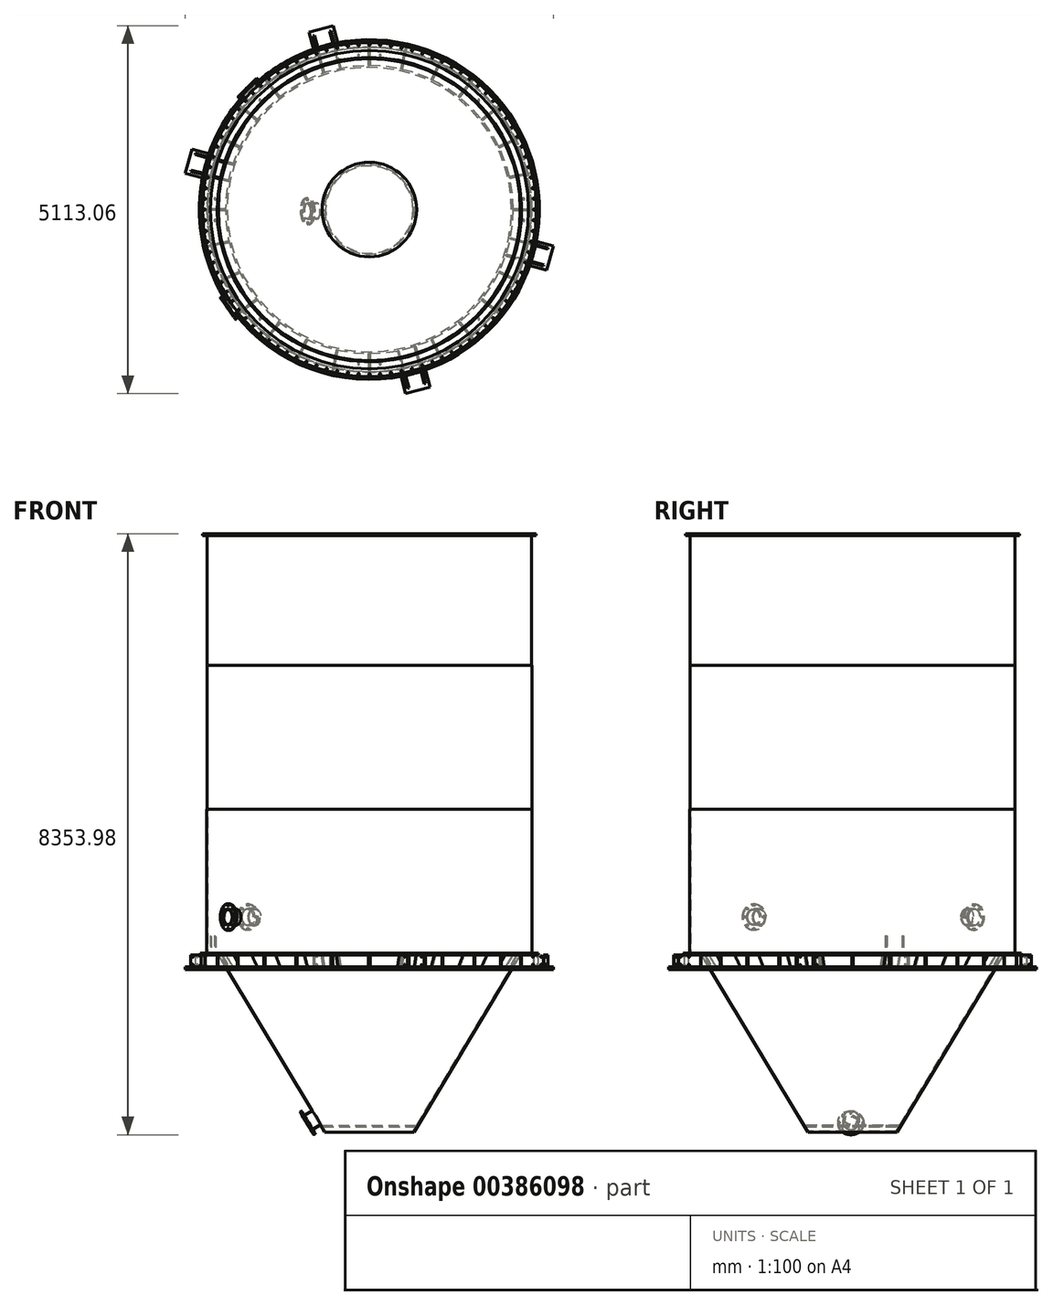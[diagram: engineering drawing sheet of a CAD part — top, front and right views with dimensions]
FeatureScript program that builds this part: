
annotation { "Feature Type Name" : "Feature", "Feature Type Description" : "" }
export const myFeature = defineFeature(function(context is Context, id is Id, definition is map)
    precondition{}
    {
        {
            var Q0;
            Q0=qCreatedBy(makeId("Front.planeOp"),FACE);
            var sketch = newSketch(context, id + "F0", { "sketchPlane" : qUnion([Q0])});
            skLineSegment(sketch, "E0", {"start": v(-2250, 0) * mm, "end": v(-2250, 5800) * mm});
            skLineSegment(sketch, "E1", {"start": v(-2256, 5800) * mm, "end": v(-2256, 4000) * mm});
            skLineSegment(sketch, "E2", {"start": v(-2256, 4000) * mm, "end": v(-2258, 4000) * mm});
            skLineSegment(sketch, "E3", {"start": v(-2258, 4000) * mm, "end": v(-2258, 2000) * mm});
            skLineSegment(sketch, "E4", {"start": v(-2258, 2000) * mm, "end": v(-2260, 2000) * mm});
            skLineSegment(sketch, "E5", {"start": v(-2260, 2000) * mm, "end": v(-2260, 0) * mm});
            skLineSegment(sketch, "E6", {"start": v(-2260, 0) * mm, "end": v(-2250, 0) * mm});
            skLineSegment(sketch, "E7", {"start": v(0, -16.96) * mm, "end": v(0, 862.75) * mm});
            skLineSegment(sketch, "E8", {"start": v(-2250, 5800) * mm, "end": v(-2212, 5800) * mm});
            skLineSegment(sketch, "E9", {"start": v(-2212, 5800) * mm, "end": v(-2212, 5828) * mm});
            skLineSegment(sketch, "E10", {"start": v(-2212, 5828) * mm, "end": v(-2320, 5828) * mm});
            skLineSegment(sketch, "E11", {"start": v(-2320, 5828) * mm, "end": v(-2320, 5800) * mm});
            skLineSegment(sketch, "E12", {"start": v(-2320, 5800) * mm, "end": v(-2256, 5800) * mm});
            skSolve(sketch);
        }
        {
            var Q0;
            Q0 = qSketchRegion(id + "F0", true);
            var Q1;
            Q1=sQuery(id+"F0.wireOp",EDGE,"E7");
            revolve(context, id + "F1", {"entities" : qUnion([Q0]), "axis" : qUnion([Q1]), "revolveType" : RevolveType.FULL});
        }
        {
            var Q0;
            Q0=qCreatedBy(makeId("Front.planeOp"),FACE);
            var sketch = newSketch(context, id + "F2", { "sketchPlane" : qUnion([Q0])});
            skLineSegment(sketch, "E13", {"start": v(-2350, 0) * mm, "end": v(-2115.02, 0) * mm});
            skLineSegment(sketch, "E14", {"start": v(-2115.02, 0) * mm, "end": v(-2100, -25) * mm});
            skLineSegment(sketch, "E15", {"start": v(-2100, -25) * mm, "end": v(-2350, -25) * mm});
            skLineSegment(sketch, "E16", {"start": v(-2350, -25) * mm, "end": v(-2350, 0) * mm});
            skLineSegment(sketch, "E17", {"start": v(0, -262.85) * mm, "end": v(0, -50.96) * mm});
            skSolve(sketch);
        }
        {
            var Q0;
            Q0 = qSketchRegion(id + "F2", true);
            var Q1;
            Q1=sQuery(id+"F2.wireOp",EDGE,"E17");
            revolve(context, id + "F3", {"operationType" : NewBodyOperationType.ADD, "entities" : qUnion([Q0]), "axis" : qUnion([Q1]), "revolveType" : RevolveType.FULL});
        }
        {
            var Q0;
            Q0=qCreatedBy(makeId("Front.planeOp"),FACE);
            var sketch = newSketch(context, id + "F4", { "sketchPlane" : qUnion([Q0])});
            skLineSegment(sketch, "E18", {"start": v(-2115.02, 0) * mm, "end": v(-620.5, -2487.3) * mm});
            skLineSegment(sketch, "E19", {"start": v(-607.64, -2479.58) * mm, "end": v(-2097.52, 0) * mm});
            skLineSegment(sketch, "E20", {"start": v(-2097.52, 0) * mm, "end": v(-2115.02, 0) * mm});
            skLineSegment(sketch, "E21", {"start": v(-620.5, -2487.3) * mm, "end": v(-607.64, -2479.58) * mm});
            skLineSegment(sketch, "E22", {"start": v(-647.98, -2412.44) * mm, "end": v(-657, -2397.44) * mm});
            skLineSegment(sketch, "E23", {"start": v(-657, -2397.44) * mm, "end": v(0, -2397.44) * mm});
            skLineSegment(sketch, "E24", {"start": v(0, -2397.44) * mm, "end": v(0, -2412.44) * mm});
            skLineSegment(sketch, "E25", {"start": v(0, -2412.44) * mm, "end": v(-647.98, -2412.44) * mm});
            skPoint(sketch, "E26", {"position": v(-1026, -1812.44) * mm});
            skSolve(sketch);
        }
        {
            var Q0;
            Q0 = qSketchRegion(id + "F4", true);
            var Q1;
            Q1=sQuery(id+"F0.wireOp",EDGE,"E7");
            revolve(context, id + "F5", {"entities" : qUnion([Q0]), "axis" : qUnion([Q1]), "revolveType" : RevolveType.FULL});
        }
        {
            var Q0;
            Q0=qCreatedBy(makeId("Front.planeOp"),FACE);
            var sketch = newSketch(context, id + "F6", { "sketchPlane" : qUnion([Q0])});
            skLineSegment(sketch, "E27", {"start": v(-2361.82, -190) * mm, "end": v(-2000.86, -190) * mm});
            skLineSegment(sketch, "E28", {"start": v(-2000.86, -190) * mm, "end": v(-1976.82, -230) * mm});
            skLineSegment(sketch, "E29", {"start": v(-1976.82, -230) * mm, "end": v(-2361.82, -230) * mm});
            skLineSegment(sketch, "E30", {"start": v(-2361.82, -230) * mm, "end": v(-2361.82, -190) * mm});
            skLineSegment(sketch, "E31", {"start": v(0, -406.67) * mm, "end": v(0, -308.21) * mm});
            skSolve(sketch);
        }
        {
            var Q0;
            Q0 = qSketchRegion(id + "F6", true);
            var Q1;
            Q1=sQuery(id+"F6.wireOp",EDGE,"E31");
            revolve(context, id + "F7", {"entities" : qUnion([Q0]), "axis" : qUnion([Q1]), "revolveType" : RevolveType.FULL});
        }
        {
            var Q0;
            Q0=qCreatedBy(makeId("Front.planeOp"),FACE);
            cPlane(context, id + "F8", {"entities" : qUnion([Q0]), "cplaneType" : CPlaneType.OFFSET, "offset" : 2340 * mm, "width" : 150 * mm, "height" : 150 * mm});
        }
        {
            var Q0;
            Q0=qCreatedBy(id+"F8.planeOp",FACE);
            var sketch = newSketch(context, id + "F9", { "sketchPlane" : qUnion([Q0])});
            skLineSegment(sketch, "E32", {"start": v(0, -25) * mm, "end": v(10, -25) * mm});
            skLineSegment(sketch, "E33", {"start": v(10, -25) * mm, "end": v(10, -190) * mm});
            skLineSegment(sketch, "E34", {"start": v(10, -190) * mm, "end": v(0, -190) * mm});
            skLineSegment(sketch, "E35", {"start": v(0, -190) * mm, "end": v(0, -25) * mm});
            skLineSegment(sketch, "E36.MirrorCS", {"start": v(-10, -190) * mm, "end": v(0, -190) * mm});
            skLineSegment(sketch, "E37.MirrorCS", {"start": v(0, -25) * mm, "end": v(-10, -25) * mm});
            skLineSegment(sketch, "E38.MirrorCS", {"start": v(-10, -25) * mm, "end": v(-10, -190) * mm});
            skSolve(sketch);
        }
        {
            var Q0;
            Q0=makeQuery(id+"F9.imprint","IMPRINT",FACE,{"disambiguationData":[TD([[makeQuery(id+"F9.imprint","IMPRINT",EDGE,{"derivedFrom":sQuery(id+"F9.wireOp",EDGE,"E32")}),-1.0]])]});
            var Q1;
            Q1=makeQuery(id+"F9.imprint","IMPRINT",FACE,{"disambiguationData":[TD([[makeQuery(id+"F9.imprint","IMPRINT",EDGE,{"derivedFrom":sQuery(id+"F9.wireOp",EDGE,"E35")}),1.0]])]});
            var Q2;
            Q2=makeQuery(id+"F5.opRevolve","SWEPT_FACE",FACE,{"disambiguationData":[OSD([sQuery(id+"F4.wireOp",EDGE,"E18")])]});
            extrude(context, id + "F10", {"entities" : qUnion([Q0, Q1]), "endBound" : BoundingType.UP_TO_SURFACE, "oppositeDirection" : true, "endBoundEntityFace" : qUnion([Q2]), "depth" : 25 * mm});
        }
        {
            var Q0;
            Q0=makeQuery(id+"F10.opExtrude","SWEPT_BODY",BODY,{"disambiguationData":[OSD([sQuery(id+"F9.wireOp",EDGE,"E32"),sQuery(id+"F9.wireOp",EDGE,"E33"),sQuery(id+"F9.wireOp",EDGE,"E34"),sQuery(id+"F9.wireOp",EDGE,"E36.MirrorCS"),sQuery(id+"F9.wireOp",EDGE,"E37.MirrorCS"),sQuery(id+"F9.wireOp",EDGE,"E38.MirrorCS")])]});
            var Q1;
            Q1=sQuery(id+"F0.wireOp",EDGE,"E7");
            circularPattern(context, id + "F11", {"entities" : qUnion([Q0]), "axis" : qUnion([Q1]), "angle" : 360 * degree, "instanceCount" : 28, "equalSpace" : true});
        }
        {
            var Q0;
            Q0=makeQuery(id+"F1.opRevolve","SWEPT_FACE",FACE,{"disambiguationData":[OSD([sQuery(id+"F0.wireOp",EDGE,"E10")])]});
            var sketch = newSketch(context, id + "F12", { "sketchPlane" : qUnion([Q0])});
            skCircle(sketch, "E39", {"center": v(-2290, 0) * mm, "radius": 10 * mm});
            skCircle(sketch, "E40.1.0", {"center": v(-2285.1, -149.77) * mm, "radius": 10 * mm});
            skCircle(sketch, "E40.2.0", {"center": v(-2270.4, -298.9) * mm, "radius": 10 * mm});
            skCircle(sketch, "E40.3.0", {"center": v(-2246, -446.76) * mm, "radius": 10 * mm});
            skCircle(sketch, "E40.4.0", {"center": v(-2211.97, -592.7) * mm, "radius": 10 * mm});
            skCircle(sketch, "E40.5.0", {"center": v(-2168.47, -736.1) * mm, "radius": 10 * mm});
            skCircle(sketch, "E40.6.0", {"center": v(-2115.68, -876.35) * mm, "radius": 10 * mm});
            skCircle(sketch, "E40.7.0", {"center": v(-2053.84, -1012.84) * mm, "radius": 10 * mm});
            skCircle(sketch, "E40.8.0", {"center": v(-1983.2, -1145) * mm, "radius": 10 * mm});
            skCircle(sketch, "E40.9.0", {"center": v(-1904.07, -1272.26) * mm, "radius": 10 * mm});
            skCircle(sketch, "E40.10.0", {"center": v(-1816.78, -1394.06) * mm, "radius": 10 * mm});
            skCircle(sketch, "E40.11.0", {"center": v(-1721.71, -1509.9) * mm, "radius": 10 * mm});
            skCircle(sketch, "E40.12.0", {"center": v(-1619.27, -1619.27) * mm, "radius": 10 * mm});
            skCircle(sketch, "E40.13.0", {"center": v(-1509.9, -1721.71) * mm, "radius": 10 * mm});
            skCircle(sketch, "E40.14.0", {"center": v(-1394.06, -1816.78) * mm, "radius": 10 * mm});
            skCircle(sketch, "E40.15.0", {"center": v(-1272.26, -1904.07) * mm, "radius": 10 * mm});
            skCircle(sketch, "E40.16.0", {"center": v(-1145, -1983.2) * mm, "radius": 10 * mm});
            skCircle(sketch, "E40.17.0", {"center": v(-1012.84, -2053.84) * mm, "radius": 10 * mm});
            skCircle(sketch, "E40.18.0", {"center": v(-876.35, -2115.68) * mm, "radius": 10 * mm});
            skCircle(sketch, "E40.19.0", {"center": v(-736.1, -2168.47) * mm, "radius": 10 * mm});
            skCircle(sketch, "E40.20.0", {"center": v(-592.7, -2211.97) * mm, "radius": 10 * mm});
            skCircle(sketch, "E40.21.0", {"center": v(-446.76, -2246) * mm, "radius": 10 * mm});
            skCircle(sketch, "E40.22.0", {"center": v(-298.9, -2270.4) * mm, "radius": 10 * mm});
            skCircle(sketch, "E40.23.0", {"center": v(-149.77, -2285.1) * mm, "radius": 10 * mm});
            skCircle(sketch, "E40.24.0", {"center": v(0, -2290) * mm, "radius": 10 * mm});
            skCircle(sketch, "E40.25.0", {"center": v(149.77, -2285.1) * mm, "radius": 10 * mm});
            skCircle(sketch, "E40.26.0", {"center": v(298.9, -2270.4) * mm, "radius": 10 * mm});
            skCircle(sketch, "E40.27.0", {"center": v(446.76, -2246) * mm, "radius": 10 * mm});
            skCircle(sketch, "E40.28.0", {"center": v(592.7, -2211.97) * mm, "radius": 10 * mm});
            skCircle(sketch, "E40.29.0", {"center": v(736.1, -2168.47) * mm, "radius": 10 * mm});
            skCircle(sketch, "E40.30.0", {"center": v(876.35, -2115.68) * mm, "radius": 10 * mm});
            skCircle(sketch, "E40.31.0", {"center": v(1012.84, -2053.84) * mm, "radius": 10 * mm});
            skCircle(sketch, "E40.32.0", {"center": v(1145, -1983.2) * mm, "radius": 10 * mm});
            skCircle(sketch, "E40.33.0", {"center": v(1272.26, -1904.07) * mm, "radius": 10 * mm});
            skCircle(sketch, "E40.34.0", {"center": v(1394.06, -1816.78) * mm, "radius": 10 * mm});
            skCircle(sketch, "E40.35.0", {"center": v(1509.9, -1721.71) * mm, "radius": 10 * mm});
            skCircle(sketch, "E40.36.0", {"center": v(1619.27, -1619.27) * mm, "radius": 10 * mm});
            skCircle(sketch, "E40.37.0", {"center": v(1721.71, -1509.9) * mm, "radius": 10 * mm});
            skCircle(sketch, "E40.38.0", {"center": v(1816.78, -1394.06) * mm, "radius": 10 * mm});
            skCircle(sketch, "E40.39.0", {"center": v(1904.07, -1272.26) * mm, "radius": 10 * mm});
            skCircle(sketch, "E40.40.0", {"center": v(1983.2, -1145) * mm, "radius": 10 * mm});
            skCircle(sketch, "E40.41.0", {"center": v(2053.84, -1012.84) * mm, "radius": 10 * mm});
            skCircle(sketch, "E40.42.0", {"center": v(2115.68, -876.35) * mm, "radius": 10 * mm});
            skCircle(sketch, "E40.43.0", {"center": v(2168.47, -736.1) * mm, "radius": 10 * mm});
            skCircle(sketch, "E40.44.0", {"center": v(2211.97, -592.7) * mm, "radius": 10 * mm});
            skCircle(sketch, "E40.45.0", {"center": v(2246, -446.76) * mm, "radius": 10 * mm});
            skCircle(sketch, "E40.46.0", {"center": v(2270.4, -298.9) * mm, "radius": 10 * mm});
            skCircle(sketch, "E40.47.0", {"center": v(2285.1, -149.77) * mm, "radius": 10 * mm});
            skCircle(sketch, "E40.48.0", {"center": v(2290, 0) * mm, "radius": 10 * mm});
            skCircle(sketch, "E40.49.0", {"center": v(2285.1, 149.77) * mm, "radius": 10 * mm});
            skCircle(sketch, "E40.50.0", {"center": v(2270.4, 298.9) * mm, "radius": 10 * mm});
            skCircle(sketch, "E40.51.0", {"center": v(2246, 446.76) * mm, "radius": 10 * mm});
            skCircle(sketch, "E40.52.0", {"center": v(2211.97, 592.7) * mm, "radius": 10 * mm});
            skCircle(sketch, "E40.53.0", {"center": v(2168.47, 736.1) * mm, "radius": 10 * mm});
            skCircle(sketch, "E40.54.0", {"center": v(2115.68, 876.35) * mm, "radius": 10 * mm});
            skCircle(sketch, "E40.55.0", {"center": v(2053.84, 1012.84) * mm, "radius": 10 * mm});
            skCircle(sketch, "E40.56.0", {"center": v(1983.2, 1145) * mm, "radius": 10 * mm});
            skCircle(sketch, "E40.57.0", {"center": v(1904.07, 1272.26) * mm, "radius": 10 * mm});
            skCircle(sketch, "E40.58.0", {"center": v(1816.78, 1394.06) * mm, "radius": 10 * mm});
            skCircle(sketch, "E40.59.0", {"center": v(1721.71, 1509.9) * mm, "radius": 10 * mm});
            skCircle(sketch, "E40.60.0", {"center": v(1619.27, 1619.27) * mm, "radius": 10 * mm});
            skCircle(sketch, "E40.61.0", {"center": v(1509.9, 1721.71) * mm, "radius": 10 * mm});
            skCircle(sketch, "E40.62.0", {"center": v(1394.06, 1816.78) * mm, "radius": 10 * mm});
            skCircle(sketch, "E40.63.0", {"center": v(1272.26, 1904.07) * mm, "radius": 10 * mm});
            skCircle(sketch, "E40.64.0", {"center": v(1145, 1983.2) * mm, "radius": 10 * mm});
            skCircle(sketch, "E40.65.0", {"center": v(1012.84, 2053.84) * mm, "radius": 10 * mm});
            skCircle(sketch, "E40.66.0", {"center": v(876.35, 2115.68) * mm, "radius": 10 * mm});
            skCircle(sketch, "E40.67.0", {"center": v(736.1, 2168.47) * mm, "radius": 10 * mm});
            skCircle(sketch, "E40.68.0", {"center": v(592.7, 2211.97) * mm, "radius": 10 * mm});
            skCircle(sketch, "E40.69.0", {"center": v(446.76, 2246) * mm, "radius": 10 * mm});
            skCircle(sketch, "E40.70.0", {"center": v(298.9, 2270.4) * mm, "radius": 10 * mm});
            skCircle(sketch, "E40.71.0", {"center": v(149.77, 2285.1) * mm, "radius": 10 * mm});
            skCircle(sketch, "E40.72.0", {"center": v(0, 2290) * mm, "radius": 10 * mm});
            skCircle(sketch, "E40.73.0", {"center": v(-149.77, 2285.1) * mm, "radius": 10 * mm});
            skCircle(sketch, "E40.74.0", {"center": v(-298.9, 2270.4) * mm, "radius": 10 * mm});
            skCircle(sketch, "E40.75.0", {"center": v(-446.76, 2246) * mm, "radius": 10 * mm});
            skCircle(sketch, "E40.76.0", {"center": v(-592.7, 2211.97) * mm, "radius": 10 * mm});
            skCircle(sketch, "E40.77.0", {"center": v(-736.1, 2168.47) * mm, "radius": 10 * mm});
            skCircle(sketch, "E40.78.0", {"center": v(-876.35, 2115.68) * mm, "radius": 10 * mm});
            skCircle(sketch, "E40.79.0", {"center": v(-1012.84, 2053.84) * mm, "radius": 10 * mm});
            skCircle(sketch, "E40.80.0", {"center": v(-1145, 1983.2) * mm, "radius": 10 * mm});
            skCircle(sketch, "E40.81.0", {"center": v(-1272.26, 1904.07) * mm, "radius": 10 * mm});
            skCircle(sketch, "E40.82.0", {"center": v(-1394.06, 1816.78) * mm, "radius": 10 * mm});
            skCircle(sketch, "E40.83.0", {"center": v(-1509.9, 1721.71) * mm, "radius": 10 * mm});
            skCircle(sketch, "E40.84.0", {"center": v(-1619.27, 1619.27) * mm, "radius": 10 * mm});
            skCircle(sketch, "E40.85.0", {"center": v(-1721.71, 1509.9) * mm, "radius": 10 * mm});
            skCircle(sketch, "E40.86.0", {"center": v(-1816.78, 1394.06) * mm, "radius": 10 * mm});
            skCircle(sketch, "E40.87.0", {"center": v(-1904.07, 1272.26) * mm, "radius": 10 * mm});
            skCircle(sketch, "E40.88.0", {"center": v(-1983.2, 1145) * mm, "radius": 10 * mm});
            skCircle(sketch, "E40.89.0", {"center": v(-2053.84, 1012.84) * mm, "radius": 10 * mm});
            skCircle(sketch, "E40.90.0", {"center": v(-2115.68, 876.35) * mm, "radius": 10 * mm});
            skCircle(sketch, "E40.91.0", {"center": v(-2168.47, 736.1) * mm, "radius": 10 * mm});
            skCircle(sketch, "E40.92.0", {"center": v(-2211.97, 592.7) * mm, "radius": 10 * mm});
            skCircle(sketch, "E40.93.0", {"center": v(-2246, 446.76) * mm, "radius": 10 * mm});
            skCircle(sketch, "E40.94.0", {"center": v(-2270.4, 298.9) * mm, "radius": 10 * mm});
            skCircle(sketch, "E40.95.0", {"center": v(-2285.1, 149.77) * mm, "radius": 10 * mm});
            skPoint(sketch, "E40.center", {"position": v(0, 0) * mm});
            skSolve(sketch);
        }
        {
            var Q0;
            Q0 = qSketchRegion(id + "F12", true);
            var Q1;
            Q1=makeQuery(id+"F1.opRevolve","SWEPT_FACE",FACE,{"disambiguationData":[OSD([sQuery(id+"F0.wireOp",EDGE,"E12")])]});
            extrude(context, id + "F13", {"entities" : qUnion([Q0]), "operationType" : NewBodyOperationType.REMOVE, "endBound" : BoundingType.UP_TO_SURFACE, "oppositeDirection" : true, "endBoundEntityFace" : qUnion([Q1]), "depth" : 25 * mm});
        }
        {
            var Q0;
            Q0=makeQuery(id+"F7.opRevolve","SWEPT_FACE",FACE,{"disambiguationData":[OSD([sQuery(id+"F6.wireOp",EDGE,"E27")])]});
            var sketch = newSketch(context, id + "F14", { "sketchPlane" : qUnion([Q0])});
            skCircle(sketch, "E41", {"center": v(-2144.76, 149.98) * mm, "radius": 12.5 * mm});
            skPoint(sketch, "E42", {"position": v(0, 0) * mm});
            skLineSegment(sketch, "E43", {"start": v(0, 0) * mm, "end": v(-2144.76, 149.98) * mm});
            skLineSegment(sketch, "E44", {"start": v(-2144.76, 0) * mm, "end": v(0, 0) * mm});
            skCircle(sketch, "E45.MirrorC", {"center": v(-2144.76, -149.98) * mm, "radius": 12.5 * mm});
            skCircle(sketch, "E46", {"center": v(-1520.28, 1520.28) * mm, "radius": 12.5 * mm});
            skLineSegment(sketch, "E47", {"start": v(-1520.28, 1520.28) * mm, "end": v(0, 0) * mm});
            skLineSegment(sketch, "E48.anchor1", {"start": v(0, 0) * mm, "end": v(-2144.76, -149.98) * mm, "construction": true});
            skCircle(sketch, "E49.1.0", {"center": v(-1520.28, -1520.28) * mm, "radius": 12.5 * mm});
            skCircle(sketch, "E49.1.1", {"center": v(-149.98, -2144.76) * mm, "radius": 12.5 * mm});
            skCircle(sketch, "E49.1.2", {"center": v(149.98, -2144.76) * mm, "radius": 12.5 * mm});
            skCircle(sketch, "E49.2.0", {"center": v(1520.28, -1520.28) * mm, "radius": 12.5 * mm});
            skCircle(sketch, "E49.2.1", {"center": v(2144.76, -149.98) * mm, "radius": 12.5 * mm});
            skCircle(sketch, "E49.2.2", {"center": v(2144.76, 149.98) * mm, "radius": 12.5 * mm});
            skCircle(sketch, "E49.3.0", {"center": v(1520.28, 1520.28) * mm, "radius": 12.5 * mm});
            skCircle(sketch, "E49.3.1", {"center": v(149.98, 2144.76) * mm, "radius": 12.5 * mm});
            skCircle(sketch, "E49.3.2", {"center": v(-149.98, 2144.76) * mm, "radius": 12.5 * mm});
            skPoint(sketch, "E50", {"position": v(-2000.17, -52.38) * mm});
            skLineSegment(sketch, "E51", {"start": v(0, 0) * mm, "end": v(-2000.17, -52.38) * mm, "construction": true});
            skPoint(sketch, "E52", {"position": v(-1843.1, -1290.55) * mm});
            skLineSegment(sketch, "E53", {"start": v(0, 0) * mm, "end": v(-1843.1, -1290.55) * mm, "construction": true});
            skLineSegment(sketch, "E54", {"start": v(-1843.1, -1290.55) * mm, "end": v(-1965.96, -1376.58) * mm});
            skSolve(sketch);
        }
        {
            var Q0;
            Q0 = qSketchRegion(id + "F14", true);
            var Q1;
            Q1=makeQuery(id+"F7.opRevolve","SWEPT_FACE",FACE,{"disambiguationData":[OSD([sQuery(id+"F6.wireOp",EDGE,"E29")])]});
            extrude(context, id + "F15", {"entities" : qUnion([Q0]), "operationType" : NewBodyOperationType.REMOVE, "endBound" : BoundingType.UP_TO_SURFACE, "oppositeDirection" : true, "endBoundEntityFace" : qUnion([Q1]), "depth" : 25 * mm});
        }
        {
            var Q0;
            Q0=makeQuery(id+"F11.opPattern","COPY",BODY,{"derivedFrom":makeQuery(id+"F10.opExtrude","SWEPT_BODY",BODY,{"disambiguationData":[OSD([sQuery(id+"F9.wireOp",EDGE,"E32"),sQuery(id+"F9.wireOp",EDGE,"E33"),sQuery(id+"F9.wireOp",EDGE,"E34"),sQuery(id+"F9.wireOp",EDGE,"E36.MirrorCS"),sQuery(id+"F9.wireOp",EDGE,"E37.MirrorCS"),sQuery(id+"F9.wireOp",EDGE,"E38.MirrorCS")])]}),"instanceName":"20"});
            deleteBodies(context, id + "F16", {"entities" : qUnion([Q0])});
        }
        {
            var Q0;
            Q0=makeQuery(id+"F11.opPattern","COPY",BODY,{"derivedFrom":makeQuery(id+"F10.opExtrude","SWEPT_BODY",BODY,{"disambiguationData":[OSD([sQuery(id+"F9.wireOp",EDGE,"E32"),sQuery(id+"F9.wireOp",EDGE,"E33"),sQuery(id+"F9.wireOp",EDGE,"E34"),sQuery(id+"F9.wireOp",EDGE,"E36.MirrorCS"),sQuery(id+"F9.wireOp",EDGE,"E37.MirrorCS"),sQuery(id+"F9.wireOp",EDGE,"E38.MirrorCS")])]}),"instanceName":"15"});
            deleteBodies(context, id + "F17", {"entities" : qUnion([Q0])});
        }
        {
            var Q0;
            Q0=makeQuery(id+"F11.opPattern","COPY",BODY,{"derivedFrom":makeQuery(id+"F10.opExtrude","SWEPT_BODY",BODY,{"disambiguationData":[OSD([sQuery(id+"F9.wireOp",EDGE,"E32"),sQuery(id+"F9.wireOp",EDGE,"E33"),sQuery(id+"F9.wireOp",EDGE,"E34"),sQuery(id+"F9.wireOp",EDGE,"E36.MirrorCS"),sQuery(id+"F9.wireOp",EDGE,"E37.MirrorCS"),sQuery(id+"F9.wireOp",EDGE,"E38.MirrorCS")])]}),"instanceName":"6"});
            deleteBodies(context, id + "F18", {"entities" : qUnion([Q0])});
        }
        {
            var Q0;
            Q0=makeQuery(id+"F11.opPattern","COPY",BODY,{"derivedFrom":makeQuery(id+"F10.opExtrude","SWEPT_BODY",BODY,{"disambiguationData":[OSD([sQuery(id+"F9.wireOp",EDGE,"E32"),sQuery(id+"F9.wireOp",EDGE,"E33"),sQuery(id+"F9.wireOp",EDGE,"E34"),sQuery(id+"F9.wireOp",EDGE,"E36.MirrorCS"),sQuery(id+"F9.wireOp",EDGE,"E37.MirrorCS"),sQuery(id+"F9.wireOp",EDGE,"E38.MirrorCS")])]}),"instanceName":"1"});
            deleteBodies(context, id + "F19", {"entities" : qUnion([Q0])});
        }
        {
            var Q0;
            Q0=makeQuery(id+"F14.imprint","IMPRINT",FACE,{"disambiguationData":[TD([[makeQuery(id+"F14.imprint","IMPRINT",EDGE,{"derivedFrom":sQuery(id+"F14.wireOp",EDGE,"E41")}),-1.0]])]});
            var sketch = newSketch(context, id + "F20", { "sketchPlane" : qUnion([Q0])});
            skLineSegment(sketch, "E55", {"start": v(-1894.95, 642.34) * mm, "end": v(-2417.87, 782.45) * mm});
            skLineSegment(sketch, "E56", {"start": v(-2417.87, 782.45) * mm, "end": v(-2423.05, 763.13) * mm});
            skLineSegment(sketch, "E57", {"start": v(-2423.05, 763.13) * mm, "end": v(-1901.29, 623.33) * mm});
            skLineSegment(sketch, "E58", {"start": v(0, 0) * mm, "end": v(-1901.45, 509.5) * mm, "construction": true});
            skArc(sketch, "E59", {"start": v(-1901.29, 623.33) * mm, "mid": v(-1898.14, 632.84) * mm, "end": v(-1894.95, 642.34) * mm});
            skLineSegment(sketch, "E60.MirrorCS", {"start": v(-2485.17, 531.31) * mm, "end": v(-2479.99, 550.63) * mm});
            skArc(sketch, "E61.MirrorCS", {"start": v(-1958.23, 410.83) * mm, "mid": v(-1960.26, 401.02) * mm, "end": v(-1962.24, 391.2) * mm});
            skLineSegment(sketch, "E62.MirrorCS", {"start": v(-2479.99, 550.63) * mm, "end": v(-1958.23, 410.83) * mm});
            skLineSegment(sketch, "E63.MirrorCS", {"start": v(-1962.24, 391.2) * mm, "end": v(-2485.17, 531.31) * mm});
            skSolve(sketch);
        }
        {
            var Q0;
            Q0 = qSketchRegion(id + "F20", true);
            var Q1;
            Q1=makeQuery(id+"F5.opRevolve","SWEPT_FACE",FACE,{"disambiguationData":[OSD([sQuery(id+"F4.wireOp",EDGE,"E18")])]});
            var Q2;
            Q2=makeQuery(id+"F1.opRevolve","SWEPT_BODY",BODY,{"disambiguationData":[OSD([sQuery(id+"F0.wireOp",EDGE,"E0"),sQuery(id+"F0.wireOp",EDGE,"E1"),sQuery(id+"F0.wireOp",EDGE,"E2"),sQuery(id+"F0.wireOp",EDGE,"E3"),sQuery(id+"F0.wireOp",EDGE,"E4"),sQuery(id+"F0.wireOp",EDGE,"E5"),sQuery(id+"F0.wireOp",EDGE,"E6"),sQuery(id+"F0.wireOp",EDGE,"E8"),sQuery(id+"F0.wireOp",EDGE,"E9"),sQuery(id+"F0.wireOp",EDGE,"E10"),sQuery(id+"F0.wireOp",EDGE,"E11"),sQuery(id+"F0.wireOp",EDGE,"E12")])]});
            extrude(context, id + "F21", {"entities" : qUnion([Q0]), "endBound" : BoundingType.UP_TO_SURFACE, "endBoundEntityFace" : qUnion([Q1]), "endBoundEntityBody" : qUnion([Q2]), "depth" : 25 * mm});
        }
        {
            var Q0;
            Q0=makeQuery(id+"F21.opExtrude","SWEPT_FACE",FACE,{"disambiguationData":[OSD([sQuery(id+"F20.wireOp",EDGE,"E55")])]});
            var sketch = newSketch(context, id + "F22", { "sketchPlane" : qUnion([Q0])});
            skLineSegment(sketch, "E64", {"start": v(2095.97, -25) * mm, "end": v(2538, 709.5) * mm});
            skLineSegment(sketch, "E65", {"start": v(2538, 709.5) * mm, "end": v(2538, -25) * mm});
            skLineSegment(sketch, "E66", {"start": v(2538, -25) * mm, "end": v(2095.97, -25) * mm});
            skSolve(sketch);
        }
        {
            var Q0;
            Q0 = qSketchRegion(id + "F22", true);
            var Q1;
            Q1=makeQuery(id+"F21.opExtrude","SWEPT_FACE",FACE,{"disambiguationData":[OSD([sQuery(id+"F20.wireOp",EDGE,"E57")])]});
            extrude(context, id + "F23", {"entities" : qUnion([Q0]), "operationType" : NewBodyOperationType.REMOVE, "endBound" : BoundingType.UP_TO_SURFACE, "oppositeDirection" : true, "endBoundEntityFace" : qUnion([Q1]), "depth" : 25 * mm});
        }
        {
            var Q0;
            Q0=makeQuery(id+"F21.opExtrude","SWEPT_FACE",FACE,{"disambiguationData":[OSD([sQuery(id+"F20.wireOp",EDGE,"E63.MirrorCS")])]});
            var sketch = newSketch(context, id + "F24", { "sketchPlane" : qUnion([Q0])});
            skLineSegment(sketch, "E67", {"start": v(-2538, -25) * mm, "end": v(-2538, 709.5) * mm});
            skLineSegment(sketch, "E68", {"start": v(-2538, 709.5) * mm, "end": v(-2095.97, -25) * mm});
            skLineSegment(sketch, "E69", {"start": v(-2095.97, -25) * mm, "end": v(-2538, -25) * mm});
            skSolve(sketch);
        }
        {
            var Q0;
            Q0 = qSketchRegion(id + "F24", true);
            var Q1;
            Q1=makeQuery(id+"F21.opExtrude","SWEPT_FACE",FACE,{"disambiguationData":[OSD([sQuery(id+"F20.wireOp",EDGE,"E62.MirrorCS")])]});
            extrude(context, id + "F25", {"entities" : qUnion([Q0]), "operationType" : NewBodyOperationType.REMOVE, "endBound" : BoundingType.UP_TO_SURFACE, "oppositeDirection" : true, "endBoundEntityFace" : qUnion([Q1]), "depth" : 25 * mm});
        }
        {
            var Q0;
            Q0=makeQuery(id+"F14.imprint","IMPRINT",FACE,{"disambiguationData":[TD([[makeQuery(id+"F14.imprint","IMPRINT",EDGE,{"derivedFrom":sQuery(id+"F14.wireOp",EDGE,"E41")}),-1.0]])]});
            var sketch = newSketch(context, id + "F26", { "sketchPlane" : qUnion([Q0])});
            skLineSegment(sketch, "E70", {"start": v(-2229.78, 778.64) * mm, "end": v(-2465.94, 841.92) * mm});
            skLineSegment(sketch, "E71", {"start": v(-2465.94, 841.92) * mm, "end": v(-2556.53, 503.85) * mm});
            skLineSegment(sketch, "E72", {"start": v(-2556.53, 503.85) * mm, "end": v(-2320.37, 440.57) * mm});
            skArc(sketch, "E73", {"start": v(-2320.37, 440.57) * mm, "mid": v(-2281.35, 611.28) * mm, "end": v(-2229.78, 778.64) * mm});
            skLineSegment(sketch, "E74", {"start": v(-2569.47, 688.49) * mm, "end": v(-1845.7, 494.55) * mm, "construction": true});
            skSolve(sketch);
        }
        {
            var Q0;
            Q0 = qSketchRegion(id + "F26", true);
            var Q1;
            Q1=makeQuery(id+"F7.opRevolve","SWEPT_FACE",FACE,{"disambiguationData":[OSD([sQuery(id+"F6.wireOp",EDGE,"E29")])]});
            extrude(context, id + "F27", {"entities" : qUnion([Q0]), "endBound" : BoundingType.UP_TO_SURFACE, "oppositeDirection" : true, "endBoundEntityFace" : qUnion([Q1]), "depth" : 25 * mm});
        }
        {
            var Q0;
            Q0=makeQuery(id+"F21.opExtrude","SWEPT_FACE",FACE,{"disambiguationData":[OSD([sQuery(id+"F20.wireOp",EDGE,"E63.MirrorCS")])]});
            var sketch = newSketch(context, id + "F28", { "sketchPlane" : qUnion([Q0])});
            skCircle(sketch, "E75", {"center": v(-2508, -50) * mm, "radius": 10 * mm});
            skCircle(sketch, "E76", {"center": v(-2388, -50) * mm, "radius": 10 * mm});
            skCircle(sketch, "E77", {"center": v(-2388, -165) * mm, "radius": 10 * mm});
            skCircle(sketch, "E78", {"center": v(-2508, -165) * mm, "radius": 10 * mm});
            skSolve(sketch);
        }
        {
            var Q0;
            Q0 = qSketchRegion(id + "F28", true);
            var Q1;
            Q1=makeQuery(id+"F21.opExtrude","SWEPT_FACE",FACE,{"disambiguationData":[OSD([sQuery(id+"F20.wireOp",EDGE,"E55")])]});
            extrude(context, id + "F29", {"entities" : qUnion([Q0]), "operationType" : NewBodyOperationType.REMOVE, "endBound" : BoundingType.UP_TO_SURFACE, "oppositeDirection" : true, "endBoundEntityFace" : qUnion([Q1]), "depth" : 25 * mm});
        }
        {
            var Q0;
            Q0=makeQuery(id+"F21.opExtrude","SWEPT_BODY",BODY,{"disambiguationData":[OSD([sQuery(id+"F20.wireOp",EDGE,"E60.MirrorCS"),sQuery(id+"F20.wireOp",EDGE,"E61.MirrorCS"),sQuery(id+"F20.wireOp",EDGE,"E62.MirrorCS"),sQuery(id+"F20.wireOp",EDGE,"E63.MirrorCS")])]});
            var Q1;
            Q1=makeQuery(id+"F27.opExtrude","SWEPT_BODY",BODY,{"disambiguationData":[OSD([sQuery(id+"F26.wireOp",EDGE,"E70"),sQuery(id+"F26.wireOp",EDGE,"E71"),sQuery(id+"F26.wireOp",EDGE,"E72"),sQuery(id+"F26.wireOp",EDGE,"E73")])]});
            var Q2;
            Q2=makeQuery(id+"F21.opExtrude","SWEPT_BODY",BODY,{"disambiguationData":[OSD([sQuery(id+"F20.wireOp",EDGE,"E55"),sQuery(id+"F20.wireOp",EDGE,"E56"),sQuery(id+"F20.wireOp",EDGE,"E57"),sQuery(id+"F20.wireOp",EDGE,"E59")])]});
            var Q3;
            Q3=sQuery(id+"F0.wireOp",EDGE,"E7");
            circularPattern(context, id + "F30", {"entities" : qUnion([Q0, Q1, Q2]), "axis" : qUnion([Q3]), "angle" : 60 * degree, "instanceCount" : 2, "oppositeDirection" : true, "equalSpace" : true});
        }
        {
            var Q0;
            Q0=makeQuery(id+"F30.opPattern","COPY",BODY,{"derivedFrom":makeQuery(id+"F27.opExtrude","SWEPT_BODY",BODY,{"disambiguationData":[OSD([sQuery(id+"F26.wireOp",EDGE,"E70"),sQuery(id+"F26.wireOp",EDGE,"E71"),sQuery(id+"F26.wireOp",EDGE,"E72"),sQuery(id+"F26.wireOp",EDGE,"E73")])]}),"instanceName":"1"});
            var Q1;
            Q1=makeQuery(id+"F30.opPattern","COPY",BODY,{"derivedFrom":makeQuery(id+"F21.opExtrude","SWEPT_BODY",BODY,{"disambiguationData":[OSD([sQuery(id+"F20.wireOp",EDGE,"E60.MirrorCS"),sQuery(id+"F20.wireOp",EDGE,"E61.MirrorCS"),sQuery(id+"F20.wireOp",EDGE,"E62.MirrorCS"),sQuery(id+"F20.wireOp",EDGE,"E63.MirrorCS")])]}),"instanceName":"1"});
            var Q2;
            Q2=makeQuery(id+"F30.opPattern","COPY",BODY,{"derivedFrom":makeQuery(id+"F21.opExtrude","SWEPT_BODY",BODY,{"disambiguationData":[OSD([sQuery(id+"F20.wireOp",EDGE,"E55"),sQuery(id+"F20.wireOp",EDGE,"E56"),sQuery(id+"F20.wireOp",EDGE,"E57"),sQuery(id+"F20.wireOp",EDGE,"E59")])]}),"instanceName":"1"});
            var Q3;
            Q3=sQuery(id+"F0.wireOp",EDGE,"E7");
            circularPattern(context, id + "F31", {"entities" : qUnion([Q0, Q1, Q2]), "axis" : qUnion([Q3]), "angle" : 120 * degree, "instanceCount" : 2, "oppositeDirection" : true, "equalSpace" : true});
        }
        {
            var Q0;
            Q0=makeQuery(id+"F31.opPattern","COPY",BODY,{"derivedFrom":makeQuery(id+"F30.opPattern","COPY",BODY,{"derivedFrom":makeQuery(id+"F27.opExtrude","SWEPT_BODY",BODY,{"disambiguationData":[OSD([sQuery(id+"F26.wireOp",EDGE,"E70"),sQuery(id+"F26.wireOp",EDGE,"E71"),sQuery(id+"F26.wireOp",EDGE,"E72"),sQuery(id+"F26.wireOp",EDGE,"E73")])]}),"instanceName":"1"}),"instanceName":"1"});
            var Q1;
            Q1=makeQuery(id+"F31.opPattern","COPY",BODY,{"derivedFrom":makeQuery(id+"F30.opPattern","COPY",BODY,{"derivedFrom":makeQuery(id+"F21.opExtrude","SWEPT_BODY",BODY,{"disambiguationData":[OSD([sQuery(id+"F20.wireOp",EDGE,"E60.MirrorCS"),sQuery(id+"F20.wireOp",EDGE,"E61.MirrorCS"),sQuery(id+"F20.wireOp",EDGE,"E62.MirrorCS"),sQuery(id+"F20.wireOp",EDGE,"E63.MirrorCS")])]}),"instanceName":"1"}),"instanceName":"1"});
            var Q2;
            Q2=makeQuery(id+"F31.opPattern","COPY",BODY,{"derivedFrom":makeQuery(id+"F30.opPattern","COPY",BODY,{"derivedFrom":makeQuery(id+"F21.opExtrude","SWEPT_BODY",BODY,{"disambiguationData":[OSD([sQuery(id+"F20.wireOp",EDGE,"E55"),sQuery(id+"F20.wireOp",EDGE,"E56"),sQuery(id+"F20.wireOp",EDGE,"E57"),sQuery(id+"F20.wireOp",EDGE,"E59")])]}),"instanceName":"1"}),"instanceName":"1"});
            var Q3;
            Q3=sQuery(id+"F0.wireOp",EDGE,"E7");
            circularPattern(context, id + "F32", {"entities" : qUnion([Q0, Q1, Q2]), "axis" : qUnion([Q3]), "angle" : 60 * degree, "instanceCount" : 2, "oppositeDirection" : true, "equalSpace" : true});
        }
        {
            var Q0;
            Q0=sQuery(id+"F14.wireOp",VERTEX,"E54.end");
            var Q1;
            Q1=sQuery(id+"F14.wireOp",EDGE,"E54");
            cPlane(context, id + "F33", {"entities" : qUnion([Q0, Q1]), "cplaneType" : CPlaneType.LINE_POINT, "offset" : 25 * mm, "width" : 150 * mm, "height" : 150 * mm});
        }
        {
            var Q0;
            Q0=qCreatedBy(id+"F33.planeOp",FACE);
            var sketch = newSketch(context, id + "F34", { "sketchPlane" : qUnion([Q0])});
            skCircle(sketch, "E79", {"center": v(0, 500) * mm, "radius": 102.5 * mm});
            skCircle(sketch, "E80", {"center": v(0, 500) * mm, "radius": 112.5 * mm});
            skSolve(sketch);
        }
        {
            var Q0;
            Q0 = qSketchRegion(id + "F34", true);
            var Q1;
            Q1=makeQuery(id+"F1.opRevolve","SWEPT_FACE",FACE,{"disambiguationData":[OSD([sQuery(id+"F0.wireOp",EDGE,"E5")])]});
            extrude(context, id + "F35", {"entities" : qUnion([Q0]), "operationType" : NewBodyOperationType.ADD, "endBound" : BoundingType.UP_TO_SURFACE, "oppositeDirection" : true, "endBoundEntityFace" : qUnion([Q1]), "depth" : 25 * mm});
        }
        {
            var Q0;
            Q0=qCreatedBy(id+"F33.planeOp",FACE);
            var sketch = newSketch(context, id + "F36", { "sketchPlane" : qUnion([Q0])});
            skCircle(sketch, "E81", {"center": v(0, 500) * mm, "radius": 185 * mm});
            skCircle(sketch, "E82", {"center": v(0, 662.5) * mm, "radius": 11 * mm});
            skPoint(sketch, "E83.center", {"position": v(0, 0) * mm});
            skCircle(sketch, "E84.1.0", {"center": v(-114.9, 614.9) * mm, "radius": 11 * mm});
            skCircle(sketch, "E84.2.0", {"center": v(-162.5, 500) * mm, "radius": 11 * mm});
            skCircle(sketch, "E84.3.0", {"center": v(-114.9, 385.1) * mm, "radius": 11 * mm});
            skCircle(sketch, "E84.4.0", {"center": v(0, 337.5) * mm, "radius": 11 * mm});
            skCircle(sketch, "E84.5.0", {"center": v(114.9, 385.1) * mm, "radius": 11 * mm});
            skCircle(sketch, "E84.6.0", {"center": v(162.5, 500) * mm, "radius": 11 * mm});
            skCircle(sketch, "E84.7.0", {"center": v(114.9, 614.9) * mm, "radius": 11 * mm});
            skCircle(sketch, "E85", {"center": v(0, 500) * mm, "radius": 112.5 * mm});
            skSolve(sketch);
        }
        {
            var Q0;
            Q0 = qSketchRegion(id + "F36", true);
            extrude(context, id + "F37", {"entities" : qUnion([Q0]), "oppositeDirection" : true, "depth" : 25 * mm});
        }
        {
            var Q0;
            Q0=sQuery(id+"F14.wireOp",VERTEX,"E50");
            var Q1;
            Q1=sQuery(id+"F14.wireOp",VERTEX,"E42");
            var Q2;
            Q2=sQuery(id+"F2.wireOp",VERTEX,"E17.end");
            cPlane(context, id + "F38", {"entities" : qUnion([Q0, Q1, Q2]), "cplaneType" : CPlaneType.THREE_POINT, "offset" : 25 * mm, "width" : 150 * mm, "height" : 150 * mm});
        }
        {
            var Q0;
            Q0=qCreatedBy(id+"F38.planeOp",FACE);
            var sketch = newSketch(context, id + "F39", { "sketchPlane" : qUnion([Q0])});
            skLineSegment(sketch, "E86", {"start": v(867.53, -2367.4) * mm, "end": v(738.96, -2290.15) * mm});
            skLineSegment(sketch, "E87", {"start": v(-620.5, -2487.3) * mm, "end": v(-2115.02, 0) * mm});
            skLineSegment(sketch, "E88", {"start": v(2115.02, 0) * mm, "end": v(620.5, -2487.3) * mm});
            skSolve(sketch);
        }
        {
            var Q0;
            Q0=sQuery(id+"F39.wireOp",EDGE,"E86");
            var Q1;
            Q1=sQuery(id+"F39.wireOp",VERTEX,"E86.start");
            cPlane(context, id + "F40", {"entities" : qUnion([Q0, Q1]), "cplaneType" : CPlaneType.LINE_POINT, "offset" : 25 * mm, "width" : 150 * mm, "height" : 150 * mm});
        }
        {
            var Q0;
            Q0=qCreatedBy(id+"F40.planeOp",FACE);
            var sketch = newSketch(context, id + "F41", { "sketchPlane" : qUnion([Q0])});
            skCircle(sketch, "E89", {"center": v(21.34, -1582.3) * mm, "radius": 102.5 * mm});
            skCircle(sketch, "E90", {"center": v(21.34, -1582.3) * mm, "radius": 112.5 * mm});
            skSolve(sketch);
        }
        {
            var Q0;
            Q0 = qSketchRegion(id + "F41", true);
            var Q1;
            Q1=makeQuery(id+"F5.opRevolve","SWEPT_FACE",FACE,{"disambiguationData":[OSD([sQuery(id+"F4.wireOp",EDGE,"E18")])]});
            extrude(context, id + "F42", {"entities" : qUnion([Q0]), "operationType" : NewBodyOperationType.ADD, "endBound" : BoundingType.UP_TO_SURFACE, "endBoundEntityFace" : qUnion([Q1]), "depth" : 25 * mm});
        }
        {
            var Q0;
            Q0=qCreatedBy(id+"F40.planeOp",FACE);
            var sketch = newSketch(context, id + "F43", { "sketchPlane" : qUnion([Q0])});
            skCircle(sketch, "E91", {"center": v(21.34, -1582.3) * mm, "radius": 112.5 * mm});
            skCircle(sketch, "E92", {"center": v(21.34, -1582.3) * mm, "radius": 185 * mm});
            skCircle(sketch, "E93", {"center": v(21.34, -1419.8) * mm, "radius": 11 * mm});
            skCircle(sketch, "E94.1.0", {"center": v(-93.56, -1467.4) * mm, "radius": 11 * mm});
            skCircle(sketch, "E94.2.0", {"center": v(-141.16, -1582.3) * mm, "radius": 11 * mm});
            skCircle(sketch, "E94.3.0", {"center": v(-93.56, -1697.21) * mm, "radius": 11 * mm});
            skCircle(sketch, "E94.4.0", {"center": v(21.34, -1744.8) * mm, "radius": 11 * mm});
            skCircle(sketch, "E94.5.0", {"center": v(136.25, -1697.21) * mm, "radius": 11 * mm});
            skCircle(sketch, "E94.6.0", {"center": v(183.84, -1582.3) * mm, "radius": 11 * mm});
            skCircle(sketch, "E94.7.0", {"center": v(136.25, -1467.4) * mm, "radius": 11 * mm});
            skSolve(sketch);
        }
        {
            var Q0;
            Q0 = qSketchRegion(id + "F43", true);
            extrude(context, id + "F44", {"entities" : qUnion([Q0]), "operationType" : NewBodyOperationType.ADD, "depth" : 25 * mm});
        }
        {
            var Q0;
            Q0=sQuery(id+"F4.wireOp",VERTEX,"E26");
            var Q1;
            Q1=qCreatedBy(makeId("Top.planeOp"),FACE);
            cPlane(context, id + "F45", {"entities" : qUnion([Q0, Q1]), "cplaneType" : CPlaneType.PLANE_POINT, "offset" : 25 * mm, "width" : 150 * mm, "height" : 150 * mm});
        }
        {
            var Q0;
            Q0=makeQuery(id+"F37.opExtrude","SWEPT_BODY",BODY,{"disambiguationData":[OSD([sQuery(id+"F36.wireOp",EDGE,"E81"),sQuery(id+"F36.wireOp",EDGE,"E82"),sQuery(id+"F36.wireOp",EDGE,"E84.1.0"),sQuery(id+"F36.wireOp",EDGE,"E84.2.0"),sQuery(id+"F36.wireOp",EDGE,"E84.3.0"),sQuery(id+"F36.wireOp",EDGE,"E84.4.0"),sQuery(id+"F36.wireOp",EDGE,"E84.5.0"),sQuery(id+"F36.wireOp",EDGE,"E84.6.0"),sQuery(id+"F36.wireOp",EDGE,"E84.7.0"),sQuery(id+"F36.wireOp",EDGE,"E85")])]});
            var Q1;
            Q1=sQuery(id+"F2.wireOp",EDGE,"E17");
            circularPattern(context, id + "F46", {"entities" : qUnion([Q0]), "axis" : qUnion([Q1]), "angle" : 80 * degree, "instanceCount" : 2, "oppositeDirection" : true, "equalSpace" : true});
        }
        {
            var Q0;
            Q0=makeQuery(id+"F46.opPattern","COPY",FACE,{"derivedFrom":makeQuery(id+"F37.opExtrude","CAP_FACE",FACE,{"disambiguationData":[OSD([sQuery(id+"F36.wireOp",EDGE,"E81"),sQuery(id+"F36.wireOp",EDGE,"E82"),sQuery(id+"F36.wireOp",EDGE,"E84.1.0"),sQuery(id+"F36.wireOp",EDGE,"E84.2.0"),sQuery(id+"F36.wireOp",EDGE,"E84.3.0"),sQuery(id+"F36.wireOp",EDGE,"E84.4.0"),sQuery(id+"F36.wireOp",EDGE,"E84.5.0"),sQuery(id+"F36.wireOp",EDGE,"E84.6.0"),sQuery(id+"F36.wireOp",EDGE,"E84.7.0"),sQuery(id+"F36.wireOp",EDGE,"E85")])],"isStart":true}),"instanceName":"1"});
            var sketch = newSketch(context, id + "F47", { "sketchPlane" : qUnion([Q0])});
            skCircle(sketch, "E95", {"center": v(0, 500) * mm, "radius": 112.5 * mm});
            skCircle(sketch, "E96", {"center": v(0, 500) * mm, "radius": 122.5 * mm});
            skSolve(sketch);
        }
        {
            var Q0;
            Q0 = qSketchRegion(id + "F47", true);
            var Q1;
            Q1=makeQuery(id+"F35.boolean.opBoolean","SPLIT",FACE,{"disambiguationData":[TD([makeQuery(id+"F1.opRevolve","SWEPT_FACE",FACE,{"disambiguationData":[OSD([sQuery(id+"F0.wireOp",EDGE,"E4")])]})])],"derivedFrom":makeQuery(id+"F1.opRevolve","SWEPT_FACE",FACE,{"disambiguationData":[OSD([sQuery(id+"F0.wireOp",EDGE,"E5")])]})});
            extrude(context, id + "F48", {"entities" : qUnion([Q0]), "operationType" : NewBodyOperationType.ADD, "endBound" : BoundingType.UP_TO_SURFACE, "oppositeDirection" : true, "endBoundEntityFace" : qUnion([Q1]), "depth" : 25 * mm});
        }
    });
